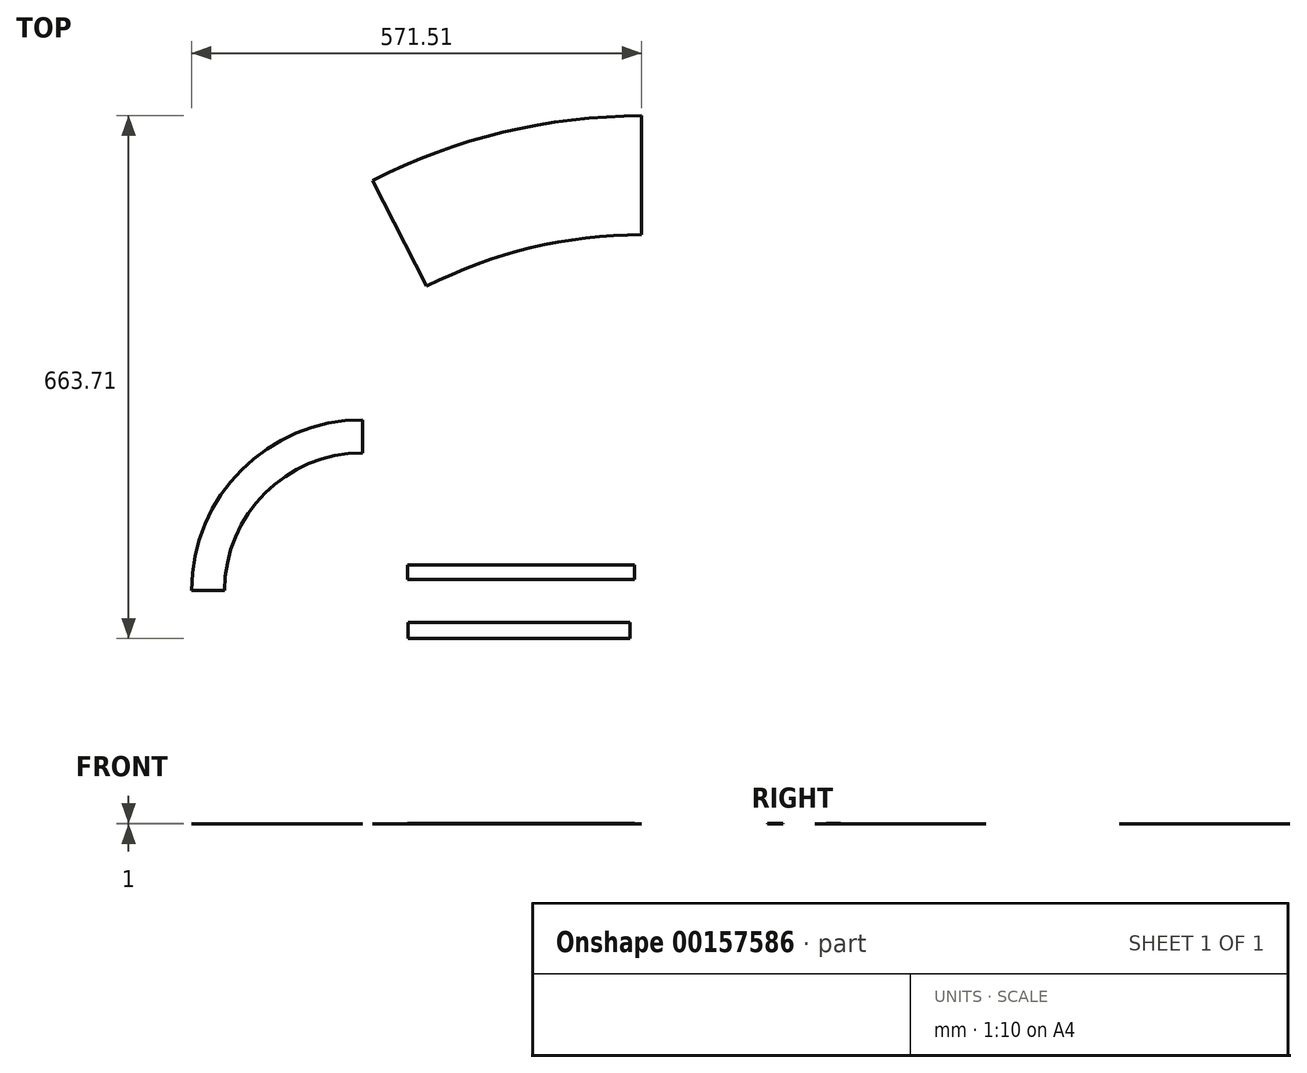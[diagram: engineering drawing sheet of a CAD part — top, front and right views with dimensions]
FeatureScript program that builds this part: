
annotation { "Feature Type Name" : "Feature", "Feature Type Description" : "" }
export const myFeature = defineFeature(function(context is Context, id is Id, definition is map)
    precondition{}
    {
        {
            var Q0;
            Q0=qCreatedBy(makeId("Top.planeOp"),FACE);
            var sketch = newSketch(context, id + "F0", { "sketchPlane" : qUnion([Q0])});
            skArc(sketch, "E0", {"start": v(0, 175) * mm, "mid": v(-123.74, 123.74) * mm, "end": v(-175, 0) * mm});
            skArc(sketch, "E1", {"start": v(0, 217) * mm, "mid": v(-153.44, 153.44) * mm, "end": v(-217, 0) * mm});
            skLineSegment(sketch, "E2", {"start": v(0, 0) * mm, "end": v(0, 217) * mm, "construction": true});
            skLineSegment(sketch, "E3", {"start": v(0, 0) * mm, "end": v(-217, 0) * mm, "construction": true});
            skLineSegment(sketch, "E4", {"start": v(-175, 0) * mm, "end": v(-217, 0) * mm});
            skLineSegment(sketch, "E5", {"start": v(0, 175) * mm, "end": v(0, 217) * mm});
            skSolve(sketch);
        }
        {
            var Q0;
            Q0=qCreatedBy(makeId("Top.planeOp"),FACE);
            var sketch = newSketch(context, id + "F1", { "sketchPlane" : qUnion([Q0])});
            skArc(sketch, "E6", {"start": v(354.5, 452.12) * mm, "mid": v(214.2, 435.51) * mm, "end": v(81.66, 386.61) * mm});
            skArc(sketch, "E7", {"start": v(354.5, 603.12) * mm, "mid": v(178.95, 582.34) * mm, "end": v(13.1, 521.15) * mm});
            skLineSegment(sketch, "E8", {"start": v(354.5, 452.12) * mm, "end": v(354.5, 603.12) * mm});
            skLineSegment(sketch, "E9", {"start": v(81.66, 386.61) * mm, "end": v(13.1, 521.15) * mm});
            skSolve(sketch);
        }
        {
            var Q0;
            Q0=makeQuery(id+"F0.imprint","IMPRINT",FACE,{"disambiguationData":[TD([[makeQuery(id+"F0.imprint","IMPRINT",EDGE,{"derivedFrom":sQuery(id+"F0.wireOp",EDGE,"E0")}),-1.0]])]});
            extrude(context, id + "F2", {"entities" : qUnion([Q0]), "depth" : .5 * mm});
        }
        {
            var Q0;
            Q0=qCreatedBy(makeId("Top.planeOp"),FACE);
            var sketch = newSketch(context, id + "F3", { "sketchPlane" : qUnion([Q0])});
            skLineSegment(sketch, "E10.bottom", {"start": v(58.1, -40.6) * mm, "end": v(340.1, -40.6) * mm});
            skLineSegment(sketch, "E10.top", {"start": v(58.1, -60.6) * mm, "end": v(340.1, -60.6) * mm});
            skLineSegment(sketch, "E10.left", {"start": v(58.1, -40.6) * mm, "end": v(58.1, -60.6) * mm});
            skLineSegment(sketch, "E10.right", {"start": v(340.1, -40.6) * mm, "end": v(340.1, -60.6) * mm});
            skLineSegment(sketch, "E11.bottom", {"start": v(57.42, 32.3) * mm, "end": v(345.42, 32.3) * mm});
            skLineSegment(sketch, "E11.top", {"start": v(57.42, 14.3) * mm, "end": v(345.42, 14.3) * mm});
            skLineSegment(sketch, "E11.left", {"start": v(57.42, 32.3) * mm, "end": v(57.42, 14.3) * mm});
            skLineSegment(sketch, "E11.right", {"start": v(345.42, 32.3) * mm, "end": v(345.42, 14.3) * mm});
            skSolve(sketch);
        }
        {
            var Q0;
            Q0=makeQuery(id+"F3.imprint","IMPRINT",FACE,{"disambiguationData":[TD([[makeQuery(id+"F3.imprint","IMPRINT",EDGE,{"derivedFrom":sQuery(id+"F3.wireOp",EDGE,"E11.bottom")}),-1.0]])]});
            var Q1;
            Q1=makeQuery(id+"F3.imprint","IMPRINT",FACE,{"disambiguationData":[TD([[makeQuery(id+"F3.imprint","IMPRINT",EDGE,{"derivedFrom":sQuery(id+"F3.wireOp",EDGE,"E10.bottom")}),-1.0]])]});
            extrude(context, id + "F4", {"entities" : qUnion([Q0, Q1]), "depth" : 1 * mm});
        }
        {
            var Q0;
            Q0=makeQuery(id+"F1.imprint","IMPRINT",FACE,{"disambiguationData":[TD([[makeQuery(id+"F1.imprint","IMPRINT",EDGE,{"derivedFrom":sQuery(id+"F1.wireOp",EDGE,"E6")}),-1.0]])]});
            extrude(context, id + "F5", {"entities" : qUnion([Q0]), "operationType" : NewBodyOperationType.ADD, "depth" : .5 * mm});
        }
    });
